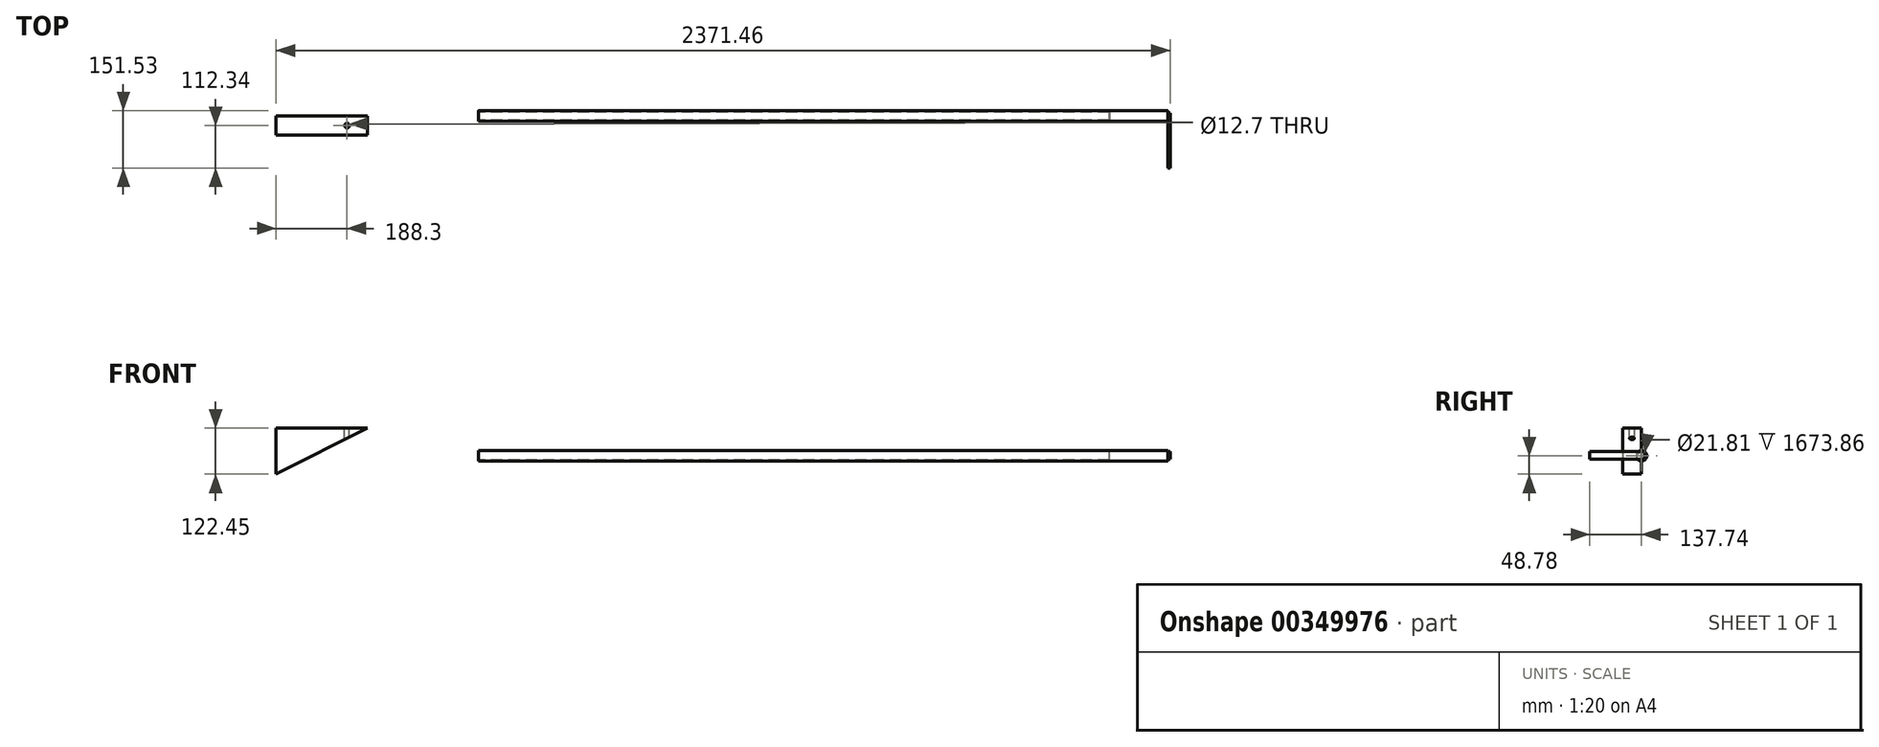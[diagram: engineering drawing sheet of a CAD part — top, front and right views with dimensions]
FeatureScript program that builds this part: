
annotation { "Feature Type Name" : "Feature", "Feature Type Description" : "" }
export const myFeature = defineFeature(function(context is Context, id is Id, definition is map)
    precondition{}
    {
        {
            var Q0;
            Q0=qCreatedBy(makeId("Right.planeOp"),FACE);
            var sketch = newSketch(context, id + "F0", { "sketchPlane" : qUnion([Q0])});
            skCircle(sketch, "E0", {"center": v(0, 0) * mm, "radius": 13.79 * mm});
            skSolve(sketch);
        }
        {
            var Q0;
            Q0 = qSketchRegion(id + "F0", true);
            extrude(context, id + "F1", {"entities" : qUnion([Q0]), "depth" : 1828.8 * mm});
        }
        {
            var Q0;
            Q0=qCreatedBy(makeId("Right.planeOp"),FACE);
            var sketch = newSketch(context, id + "F2", { "sketchPlane" : qUnion([Q0])});
            skCircle(sketch, "E1", {"center": v(0, 0) * mm, "radius": 10.9 * mm});
            skSolve(sketch);
        }
        {
            var Q0;
            Q0 = qSketchRegion(id + "F2", true);
            extrude(context, id + "F3", {"entities" : qUnion([Q0]), "operationType" : NewBodyOperationType.REMOVE, "depth" : 1673.86 * mm});
        }
        {
            var Q0;
            Q0=makeQuery(id+"F1.opExtrude","CAP_FACE",FACE,{"disambiguationData":[OSD([sQuery(id+"F0.wireOp",EDGE,"E0")])],"isStart":false});
            var sketch = newSketch(context, id + "F4", { "sketchPlane" : qUnion([Q0])});
            skLineSegment(sketch, "E2.bottom", {"start": v(8.24, 11.05) * mm, "end": v(-137.74, 11.05) * mm});
            skLineSegment(sketch, "E2.top", {"start": v(8.24, -8.31) * mm, "end": v(-137.74, -8.31) * mm});
            skLineSegment(sketch, "E2.left", {"start": v(8.24, 11.05) * mm, "end": v(8.24, -8.31) * mm});
            skLineSegment(sketch, "E2.right", {"start": v(-137.74, 11.05) * mm, "end": v(-137.74, -8.31) * mm});
            skSolve(sketch);
        }
        {
            var Q0;
            Q0 = qSketchRegion(id + "F4", true);
            extrude(context, id + "F5", {"entities" : qUnion([Q0]), "operationType" : NewBodyOperationType.ADD, "depth" : 6.35 * mm});
        }
        {
            var Q0;
            Q0=qCreatedBy(makeId("Front.planeOp"),FACE);
            var sketch = newSketch(context, id + "F6", { "sketchPlane" : qUnion([Q0])});
            skLineSegment(sketch, "E3", {"start": v(-536.31, 73.67) * mm, "end": v(-293.8, 73.67) * mm});
            skLineSegment(sketch, "E4", {"start": v(-293.8, 73.67) * mm, "end": v(-536.31, -48.78) * mm});
            skLineSegment(sketch, "E5", {"start": v(-536.31, -48.78) * mm, "end": v(-536.31, 73.67) * mm});
            skSolve(sketch);
        }
        {
            var Q0;
            Q0 = qSketchRegion(id + "F6", true);
            extrude(context, id + "F7", {"entities" : qUnion([Q0]), "depth" : 50.8 * mm, "offsetDistance" : 25.4 * mm});
        }
        {
            var Q0;
            Q0=makeQuery(id+"F7.opExtrude","SWEPT_FACE",FACE,{"disambiguationData":[OSD([sQuery(id+"F6.wireOp",EDGE,"E3")])]});
            var sketch = newSketch(context, id + "F8", { "sketchPlane" : qUnion([Q0])});
            skCircle(sketch, "E6", {"center": v(-348.01, -25.4) * mm, "radius": 6.35 * mm});
            skPoint(sketch, "E6.centerSnap0", {"position": v(-293.8, -25.4) * mm});
            skSolve(sketch);
        }
        {
            var Q0;
            Q0 = qSketchRegion(id + "F8", true);
            extrude(context, id + "F9", {"entities" : qUnion([Q0]), "operationType" : NewBodyOperationType.REMOVE, "oppositeDirection" : true, "depth" : 38.1 * mm, "offsetDistance" : 25.4 * mm});
        }
    });
